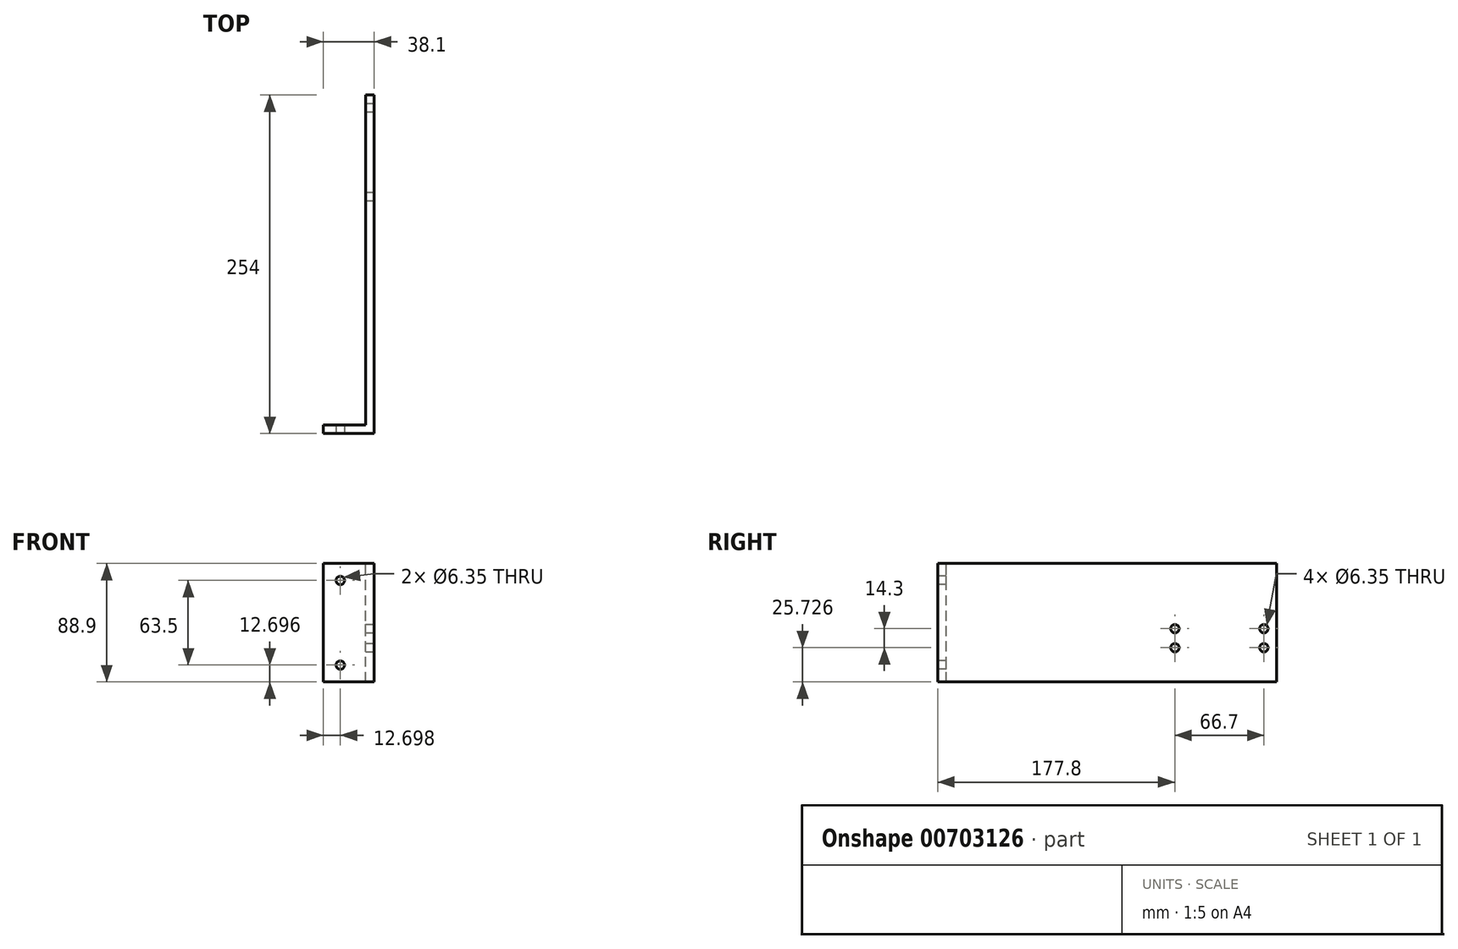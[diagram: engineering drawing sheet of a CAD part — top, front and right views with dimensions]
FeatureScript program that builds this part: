
annotation { "Feature Type Name" : "Feature", "Feature Type Description" : "" }
export const myFeature = defineFeature(function(context is Context, id is Id, definition is map)
    precondition{}
    {
        {
            var Q0;
            Q0=qCreatedBy(makeId("Front.planeOp"),FACE);
            var sketch = newSketch(context, id + "F0", { "sketchPlane" : qUnion([Q0])});
            skLineSegment(sketch, "E0.bottom", {"start": v(-12.92, 85.1) * mm, "end": v(25.18, 85.1) * mm});
            skLineSegment(sketch, "E0.top", {"start": v(-12.92, -3.8) * mm, "end": v(25.18, -3.8) * mm});
            skLineSegment(sketch, "E0.left", {"start": v(-12.92, 85.1) * mm, "end": v(-12.92, -3.8) * mm});
            skLineSegment(sketch, "E0.right", {"start": v(25.18, 85.1) * mm, "end": v(25.18, -3.8) * mm});
            skSolve(sketch);
        }
        {
            var Q0;
            Q0=qSketchRegion(id+"F0",true);
            extrude(context, id + "F1", {"entities" : qUnion([Q0]), "depth" : 6.35 * mm, "offsetDistance" : 25.4 * mm});
        }
        {
            var Q0;
            Q0=makeQuery(id+"F1.opExtrude","CAP_FACE",FACE,{"disambiguationData":[OSD([sQuery(id+"F0.wireOp",EDGE,"E0.bottom"),sQuery(id+"F0.wireOp",EDGE,"E0.top"),sQuery(id+"F0.wireOp",EDGE,"E0.left"),sQuery(id+"F0.wireOp",EDGE,"E0.right")])],"isStart":true});
            var sketch = newSketch(context, id + "F2", { "sketchPlane" : qUnion([Q0])});
            skLineSegment(sketch, "E1.bottom", {"start": v(12.92, 85.1) * mm, "end": v(6.57, 85.1) * mm});
            skLineSegment(sketch, "E1.top", {"start": v(12.92, -3.8) * mm, "end": v(6.57, -3.8) * mm});
            skLineSegment(sketch, "E1.left", {"start": v(12.92, 85.1) * mm, "end": v(12.92, -3.8) * mm});
            skLineSegment(sketch, "E1.right", {"start": v(6.57, 85.1) * mm, "end": v(6.57, -3.8) * mm});
            skLineSegment(sketch, "E2.bottom", {"start": v(-25.18, -3.8) * mm, "end": v(-18.83, -3.8) * mm});
            skLineSegment(sketch, "E2.top", {"start": v(-25.18, 85.1) * mm, "end": v(-18.83, 85.1) * mm});
            skLineSegment(sketch, "E2.left", {"start": v(-25.18, -3.8) * mm, "end": v(-25.18, 85.1) * mm});
            skLineSegment(sketch, "E2.right", {"start": v(-18.83, -3.8) * mm, "end": v(-18.83, 85.1) * mm});
            skSolve(sketch);
        }
        {
            var Q0;
            Q0=makeQuery(id+"F2.imprint","IMPRINT",FACE,{"disambiguationData":[TD([[makeQuery(id+"F2.imprint","IMPRINT",EDGE,{"derivedFrom":sQuery(id+"F2.wireOp",EDGE,"E2.bottom")}),-1.0]])]});
            extrude(context, id + "F3", {"entities" : qUnion([Q0]), "operationType" : NewBodyOperationType.ADD, "depth" : 247.65 * mm, "offsetDistance" : 25.4 * mm});
        }
        {
            var Q0;
            Q0=makeQuery(id+"F1.opExtrude","CAP_FACE",FACE,{"disambiguationData":[OSD([sQuery(id+"F0.wireOp",EDGE,"E0.bottom"),sQuery(id+"F0.wireOp",EDGE,"E0.top"),sQuery(id+"F0.wireOp",EDGE,"E0.left"),sQuery(id+"F0.wireOp",EDGE,"E0.right")])],"isStart":false});
            var sketch = newSketch(context, id + "F4", { "sketchPlane" : qUnion([Q0])});
            skPoint(sketch, "E3", {"position": v(-0.22, 8.9) * mm});
            skPoint(sketch, "E4", {"position": v(-0.22, 72.4) * mm});
            skSolve(sketch);
        }
        {
            var Q0;
            Q0=sQuery(id+"F4.wireOp",VERTEX,"E4");
            var Q1;
            Q1=sQuery(id+"F4.wireOp",VERTEX,"E3");
            var Q2;
            Q2=makeQuery(id+"F1.opExtrude","SWEPT_BODY",BODY,{"disambiguationData":[OSD([sQuery(id+"F0.wireOp",EDGE,"E0.bottom"),sQuery(id+"F0.wireOp",EDGE,"E0.top"),sQuery(id+"F0.wireOp",EDGE,"E0.left"),sQuery(id+"F0.wireOp",EDGE,"E0.right")])]});
            hole(context, id + "F5", {"style" : HoleStyle.SIMPLE, "endStyle" : HoleEndStyle.THROUGH, "holeDiameter" : 6.35 * mm, "majorDiameter" : 6.35 * mm, "isTappedThrough" : true, "tappedDepth" : 12.7 * mm, "tapClearance" : 3, "locations" : qUnion([Q0, Q1]), "scope" : qUnion([Q2])});
        }
        {
            var Q0;
            Q0=makeQuery(id+"F3.boolean.opBoolean","MERGE",FACE,{"derivedFrom":[makeQuery(id+"F1.opExtrude","SWEPT_FACE",FACE,{"disambiguationData":[OSD([sQuery(id+"F0.wireOp",EDGE,"E0.right")])]}),makeQuery(id+"F3.opExtrude","SWEPT_FACE",FACE,{"disambiguationData":[OSD([sQuery(id+"F2.wireOp",EDGE,"E2.left")])]})]});
            var sketch = newSketch(context, id + "F6", { "sketchPlane" : qUnion([Q0])});
            skPoint(sketch, "E5", {"position": v(171.45, 21.94) * mm});
            skPoint(sketch, "E6.0.1.0", {"position": v(171.45, 36.24) * mm});
            skPoint(sketch, "E6.1.0.0", {"position": v(238.15, 21.94) * mm});
            skPoint(sketch, "E6.1.1.0", {"position": v(238.15, 36.24) * mm});
            skLineSegment(sketch, "E6.direction1", {"start": v(171.45, 21.94) * mm, "end": v(238.15, 21.94) * mm, "construction": true});
            skLineSegment(sketch, "E6.direction2", {"start": v(171.45, 21.94) * mm, "end": v(171.45, 36.24) * mm, "construction": true});
            skSolve(sketch);
        }
        {
            var Q0;
            Q0=sQuery(id+"F6.wireOp",VERTEX,"E6.0.1.0");
            var Q1;
            Q1=sQuery(id+"F6.wireOp",VERTEX,"E5");
            var Q2;
            Q2=sQuery(id+"F6.wireOp",VERTEX,"E6.1.0.0");
            var Q3;
            Q3=sQuery(id+"F6.wireOp",VERTEX,"E6.1.1.0");
            var Q4;
            Q4=makeQuery(id+"F1.opExtrude","SWEPT_BODY",BODY,{"disambiguationData":[OSD([sQuery(id+"F0.wireOp",EDGE,"E0.bottom"),sQuery(id+"F0.wireOp",EDGE,"E0.top"),sQuery(id+"F0.wireOp",EDGE,"E0.left"),sQuery(id+"F0.wireOp",EDGE,"E0.right")])]});
            hole(context, id + "F7", {"style" : HoleStyle.SIMPLE, "endStyle" : HoleEndStyle.THROUGH, "holeDiameter" : 6.35 * mm, "majorDiameter" : 6.35 * mm, "isTappedThrough" : true, "tappedDepth" : 12.7 * mm, "tapClearance" : 3, "locations" : qUnion([Q0, Q1, Q2, Q3]), "scope" : qUnion([Q4])});
        }
    });
